# Revit family: BC2012
name_source: partatom
category: Generic Models
revit_build: Autodesk Revit 2014 (Build: 20140709_2115(x64)
units: mm (PartAtom-declared; Revit-internal decimal feet)

## types (1)
- BC 2012 Dolphin Hand Dryer
    Assembly Code = D2010900
    Description = Surface Mounted Hand Dryer
    Fax No. = +44 (0) 1424 205200
    Height = 700mm
    Manufacturer = Bell-Chem Products Co.
    Model = BC 2012
    Product Data = No touch APL hand dryer (cold only) +( hot switch) – low and high speed. Dries hands in ten seconds. Built in tamper proof  timer function. Two speeds and two heat settings. Built in UV sterilisation function. Power: 1650 - 2050 w. Current 8.6A. Voltage 220-240v. 50/60Hz. Actual current Max 3.51A (Cold) speed high or low. Actual current Max 3.3A (Cold) speed high. Actual current Max 2.6A (Cold) speed low. Actual current Max 7.6A Hot) speed low. Actual current Max 8.1A (Hot) speed high. GSQ70A. 230-50Hz. 850w. Actual current Max 5.1A (start up only). Actual current 4.17A (in use). 99.9% HEPA Filter. UV Sterilisation. LED Indicator. 10 second dry time. Lo-Carbon DC Motor, 750W. Air speed 95m/s. Unique blue dry zone indicator. Antibacterial coating. Heater Element 900-1300W, adjustable/ On/Off. Antibacterial dust filter. IPX4 Rated.
    Product Page Link = http://www.dolphindispensers.co.uk
    Projection = 215mm
    Tel No. = +44 (0) 1424 202224
    URL = www.dolphindispensers.co.uk
    Width = 278mm

## geometry (parser evidence)
native form markers: Sweep x1
no freeform markers — native parametric forms only
